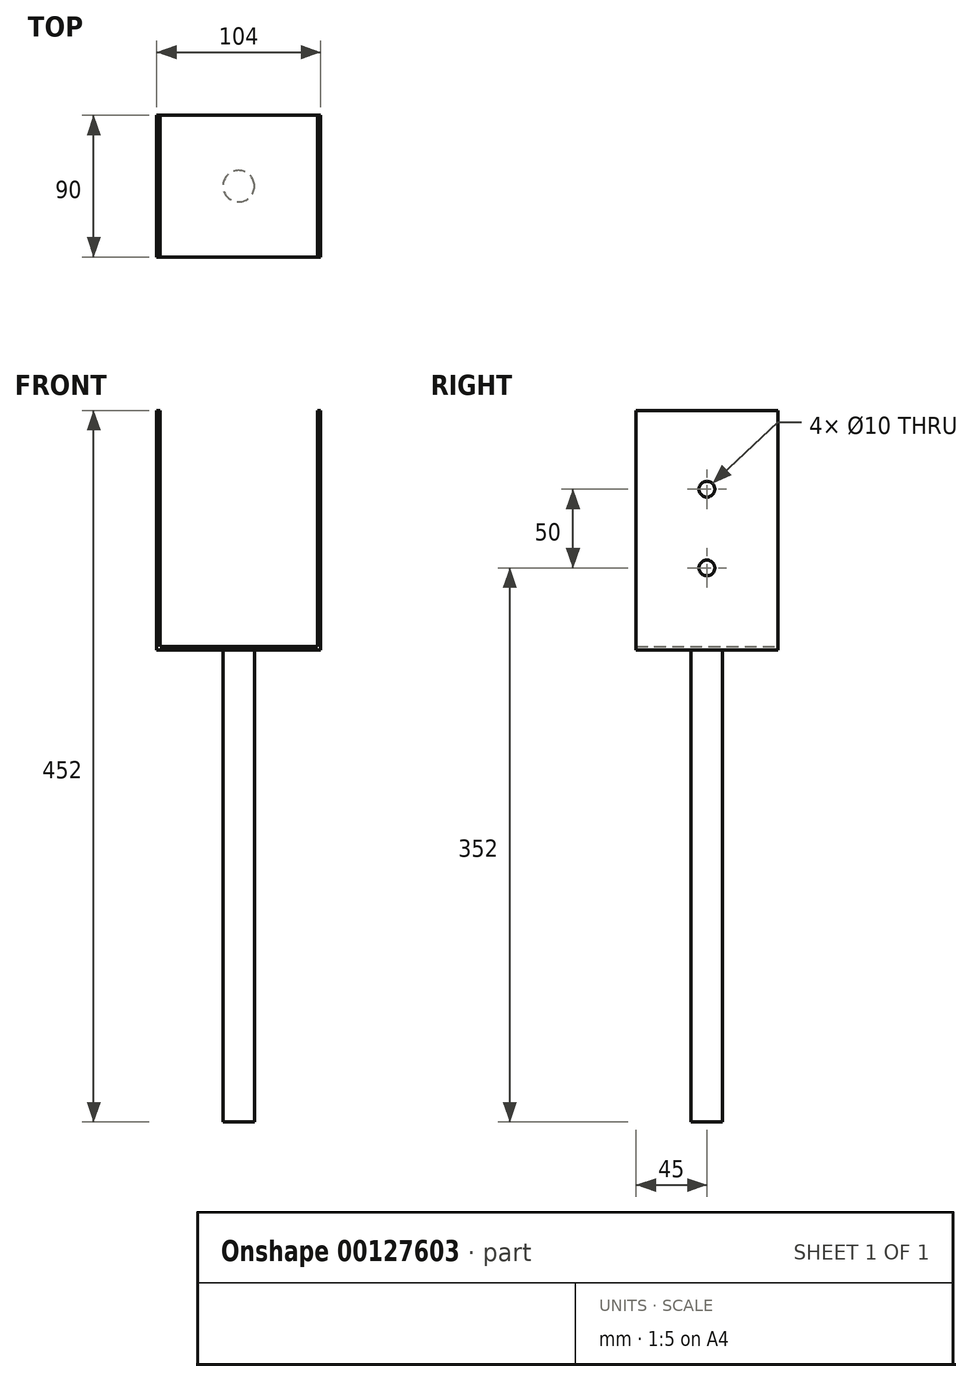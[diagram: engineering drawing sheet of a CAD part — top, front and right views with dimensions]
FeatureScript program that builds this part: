
annotation { "Feature Type Name" : "Feature", "Feature Type Description" : "" }
export const myFeature = defineFeature(function(context is Context, id is Id, definition is map)
    precondition{}
    {
        {
            var Q0;
            Q0=qCreatedBy(makeId("Front.planeOp"),FACE);
            var sketch = newSketch(context, id + "F0", { "sketchPlane" : qUnion([Q0])});
            skLineSegment(sketch, "E0", {"start": v(0, 0) * mm, "end": v(-50, 0) * mm});
            skLineSegment(sketch, "E1", {"start": v(-50, 0) * mm, "end": v(-50, 150) * mm});
            skLineSegment(sketch, "E2", {"start": v(0, 0) * mm, "end": v(50, 0) * mm});
            skLineSegment(sketch, "E3", {"start": v(50, 0) * mm, "end": v(50, 150) * mm});
            skLineSegment(sketch, "E4", {"start": v(-50, 150) * mm, "end": v(-52, 150) * mm});
            skLineSegment(sketch, "E5", {"start": v(-52, 150) * mm, "end": v(-52, -2) * mm});
            skLineSegment(sketch, "E6", {"start": v(-52, -2) * mm, "end": v(52, -2) * mm});
            skLineSegment(sketch, "E7", {"start": v(52, -2) * mm, "end": v(52, 150) * mm});
            skLineSegment(sketch, "E8", {"start": v(52, 150) * mm, "end": v(50, 150) * mm});
            skSolve(sketch);
        }
        {
            var Q0;
            Q0=makeQuery(id+"F0.imprint","IMPRINT",FACE,{"disambiguationData":[TD([[makeQuery(id+"F0.imprint","IMPRINT",EDGE,{"derivedFrom":sQuery(id+"F0.wireOp",EDGE,"E0")}),1.0]])]});
            extrude(context, id + "F1", {"entities" : qUnion([Q0]), "depth" : 90 * mm});
        }
        {
            var Q0;
            Q0=makeQuery(id+"F1.opExtrude","SWEPT_FACE",FACE,{"disambiguationData":[OSD([sQuery(id+"F0.wireOp",EDGE,"E6")])]});
            var sketch = newSketch(context, id + "F2", { "sketchPlane" : qUnion([Q0])});
            skLineSegment(sketch, "E9", {"start": v(-5.72, 45) * mm, "end": v(9.5, 45) * mm, "construction": true});
            skPoint(sketch, "E9.startSnap0", {"position": v(-52, 45) * mm});
            skCircle(sketch, "E10", {"center": v(0, 45) * mm, "radius": 10 * mm});
            skSolve(sketch);
        }
        {
            var Q0;
            Q0=makeQuery(id+"F2.imprint","IMPRINT",FACE,{"disambiguationData":[TD([[makeQuery(id+"F2.imprint","IMPRINT",EDGE,{"derivedFrom":sQuery(id+"F2.wireOp",EDGE,"E10")}),1.0]])]});
            extrude(context, id + "F3", {"entities" : qUnion([Q0]), "operationType" : NewBodyOperationType.ADD, "depth" : 300 * mm});
        }
        {
            var Q0;
            Q0=makeQuery(id+"F1.opExtrude","SWEPT_FACE",FACE,{"disambiguationData":[OSD([sQuery(id+"F0.wireOp",EDGE,"E5")])]});
            var sketch = newSketch(context, id + "F4", { "sketchPlane" : qUnion([Q0])});
            skLineSegment(sketch, "E11", {"start": v(45, 138.76) * mm, "end": v(45, 11.93) * mm, "construction": true});
            skPoint(sketch, "E11.startSnap0", {"position": v(45, 150) * mm});
            skCircle(sketch, "E12", {"center": v(45, 100) * mm, "radius": 5 * mm});
            skCircle(sketch, "E13", {"center": v(45, 50) * mm, "radius": 5 * mm});
            skSolve(sketch);
        }
        {
            var Q0;
            Q0=makeQuery(id+"F4.imprint","IMPRINT",FACE,{"disambiguationData":[TD([[makeQuery(id+"F4.imprint","IMPRINT",EDGE,{"derivedFrom":sQuery(id+"F4.wireOp",EDGE,"E12")}),1.0]])]});
            var Q1;
            Q1=makeQuery(id+"F4.imprint","IMPRINT",FACE,{"disambiguationData":[TD([[makeQuery(id+"F4.imprint","IMPRINT",EDGE,{"derivedFrom":sQuery(id+"F4.wireOp",EDGE,"E13")}),1.0]])]});
            extrude(context, id + "F5", {"entities" : qUnion([Q0, Q1]), "operationType" : NewBodyOperationType.REMOVE, "endBound" : BoundingType.THROUGH_ALL, "oppositeDirection" : true, "depth" : 25 * mm});
        }
    });
